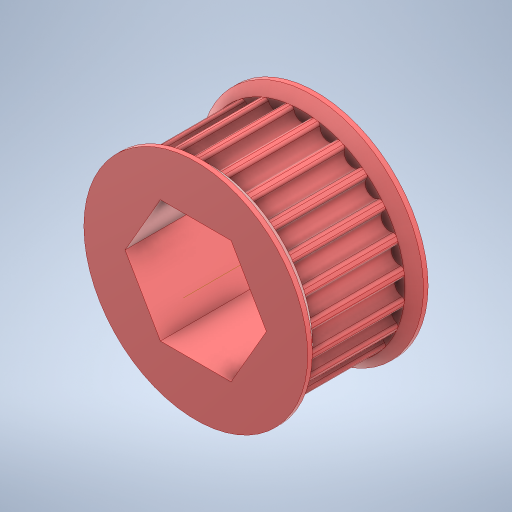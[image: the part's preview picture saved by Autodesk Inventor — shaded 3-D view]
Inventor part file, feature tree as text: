
AUTODESK INVENTOR PART (.ipt)
format: ipt  version: 2023.3 (Build 273359000, 359)  size: 491,520 bytes
history: native  units: in
note: dims shown in document units (in); Inventor stores cm internally (conversion verified against a paired STEP export)
features: extrude x7, sketch x7, mirror x2, chamfer x2, other x1, fillet x1, pattern_circular x1
ambient origin geometry x8: Origin, YZ Plane, XZ Plane, XY Plane, X Axis, Y Axis, Z Axis, Center Point
bodies: Solid1 (feature_tree)
feature tree (21):
  other  "Hex Bore"
  extrude  "HTD Base"  Depth=0.3937in TaperAngle=0.0deg
  extrude  "HTD Flange"  Depth=0.0591in
  mirror  "HTD Flanges"
  chamfer  "HTD Flange Chamfer"  Distance=0.0787in Angle=45.0deg
  extrude  "GT2 Base"  TaperAngle=0.0deg  [1 undecoded]
  extrude  "GT2 Base Tooth"  TaperAngle=0.0deg  [1 undecoded]
  fillet  "GT2 Base Tooth pt. 2"  Radius=0.8723in
  pattern_circular  "GT2 Teeth"  [2 undecoded]
  extrude  "GT2 Flange"  Depth=0.0591in
  mirror  "GT2 Flanges"
  chamfer  "GT2 Flange Chamfer"  Distance=0.0075in
  extrude  "Circle Bore"  TaperAngle=0.0deg  [1 undecoded]
  extrude  "Extrusion9"  Depth=0.0118in
  sketch  "Sketch1"  dims[d0=1.4588in d1=0.3937in d2=0.0in]
  sketch  "Sketch4"  dims[d12=0.0394in d13=0.0591in]
  sketch  "Sketch5"  dims[d14=0.0in]
  sketch  "Sketch6"  dims[d15=0.0394in d16=0.0787in d17=45.0deg]
  sketch  "Sketch7"  dims[d18=0.52in d19=0.0in d20=0.0in]
  sketch  "Sketch8"  dims[d21=0.52in d22=0.0in d23=0.0in d24=0.8723in]
  sketch  "Sketch9"  dims[d25=0.3937in d26=0.0in d27=0.0727in d28=0.0075in d29=0.0in d30=0.0in d31=0.0118in d32=9.4488in d33=360.0deg d35=0.0394in d36=0.0591in d37=0.0in d38=0.0394in d39=0.0787in d40=45.0deg d41=0.05in d42=0.4875in d43=0.0in]
note: 5 required parameter values undecoded (feature->parameter linkage not recoverable at this tier; creation-order binding heuristic only, values carry confidence <= 0.55)
